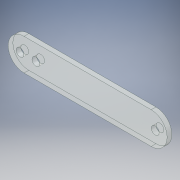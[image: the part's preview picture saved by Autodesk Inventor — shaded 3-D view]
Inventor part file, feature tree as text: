
AUTODESK INVENTOR PART (.ipt)
format: ipt  version: 2019 (Build 230136000, 136)  size: 121,344 bytes
history: native  units: in
note: dims shown in document units (in); Inventor stores cm internally (conversion verified against a paired STEP export)
features: fillet x4, extrude x2, sketch x2
ambient origin geometry x8: Origin, YZ Plane, XZ Plane, XY Plane, X Axis, Y Axis, Z Axis, Center Point
bodies: Solid1 (feature_tree)
feature tree (8):
  extrude  "Extrusion1"  Depth=0.1181in
  fillet  "Fillet1"  Radius=0.1969in
  fillet  "Fillet2"  Radius=0.1969in
  fillet  "Fillet3"  Radius=0.2953in
  fillet  "Fillet4"  Radius=0.1181in
  extrude  "Extrusion2"  Depth=0.3937in
  sketch  "Sketch1"  dims[d2=0.3937in d3=0.2953in d4=0.1969in d5=0.1969in d6=0.2953in d7=0.1181in d8=0.0in]
  sketch  "Sketch2"  dims[d9=0.3937in d10=0.3937in d11=0.3937in d12=0.3937in d16=0.0in d17=0.0in]
